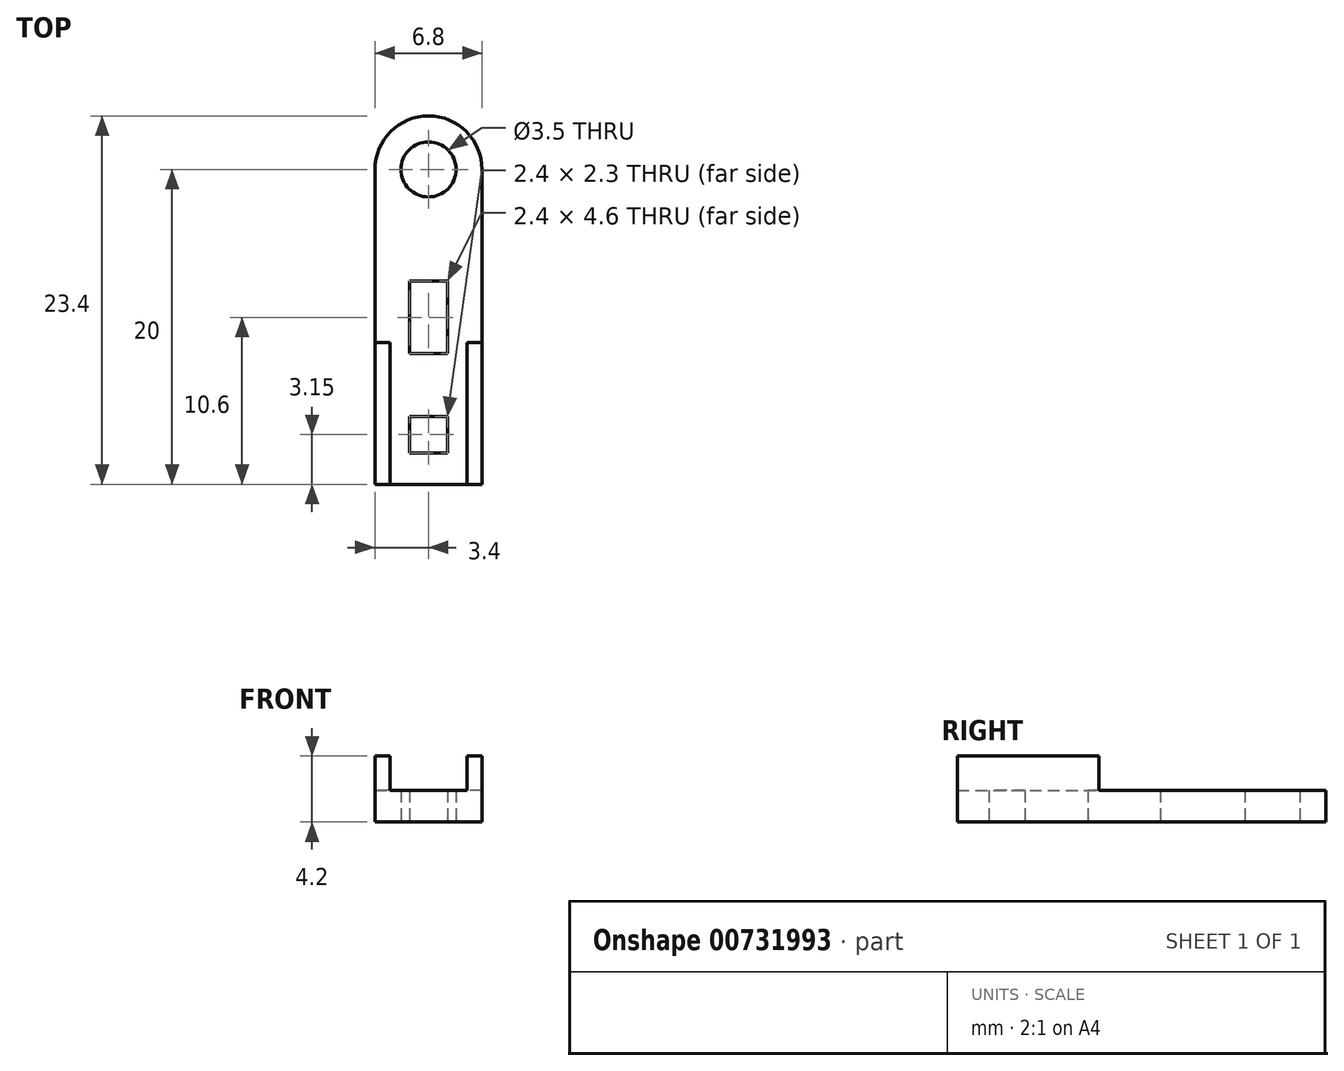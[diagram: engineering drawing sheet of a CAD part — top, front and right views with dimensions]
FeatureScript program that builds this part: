
annotation { "Feature Type Name" : "Feature", "Feature Type Description" : "" }
export const myFeature = defineFeature(function(context is Context, id is Id, definition is map)
    precondition{}
    {
        {
            var Q0;
            Q0=qCreatedBy(makeId("Top.planeOp"),FACE);
            var sketch = newSketch(context, id + "F0", { "sketchPlane" : qUnion([Q0])});
            skArc(sketch, "E0", {"start": v(3.4, 10) * mm, "mid": v(0, 13.4) * mm, "end": v(-3.4, 10) * mm});
            skLineSegment(sketch, "E1", {"start": v(-3.4, 10) * mm, "end": v(-3.4, -10) * mm});
            skLineSegment(sketch, "E2", {"start": v(-3.4, -10) * mm, "end": v(3.4, -10) * mm});
            skLineSegment(sketch, "E3", {"start": v(3.4, -10) * mm, "end": v(3.4, 10) * mm});
            skLineSegment(sketch, "E4.bottom", {"start": v(-1.2, 2.9) * mm, "end": v(1.2, 2.9) * mm});
            skLineSegment(sketch, "E4.top", {"start": v(-1.2, -1.7) * mm, "end": v(1.2, -1.7) * mm});
            skLineSegment(sketch, "E4.left", {"start": v(-1.2, 2.9) * mm, "end": v(-1.2, -1.7) * mm});
            skLineSegment(sketch, "E4.right", {"start": v(1.2, 2.9) * mm, "end": v(1.2, -1.7) * mm});
            skLineSegment(sketch, "E5.bottom", {"start": v(-1.2, -5.7) * mm, "end": v(1.2, -5.7) * mm});
            skLineSegment(sketch, "E5.top", {"start": v(-1.2, -8) * mm, "end": v(1.2, -8) * mm});
            skLineSegment(sketch, "E5.left", {"start": v(-1.2, -5.7) * mm, "end": v(-1.2, -8) * mm});
            skLineSegment(sketch, "E5.right", {"start": v(1.2, -5.7) * mm, "end": v(1.2, -8) * mm});
            skPoint(sketch, "E6", {"position": v(0, 2.9) * mm});
            skPoint(sketch, "E7", {"position": v(0, -8) * mm});
            skCircle(sketch, "E8", {"center": v(0, 10) * mm, "radius": 1.75 * mm});
            skPoint(sketch, "E9", {"position": v(-3.4, 0) * mm});
            skSolve(sketch);
        }
        {
            var Q0;
            Q0=makeQuery(id+"F0.imprint","IMPRINT",FACE,{"disambiguationData":[TD([[makeQuery(id+"F0.imprint","IMPRINT",EDGE,{"derivedFrom":sQuery(id+"F0.wireOp",EDGE,"E0")}),1.0]])]});
            extrude(context, id + "F1", {"entities" : qUnion([Q0]), "depth" : 2 * mm, "offsetDistance" : 25.4 * mm});
        }
        {
            var Q0;
            Q0=makeQuery(id+"F1.opExtrude","CAP_FACE",FACE,{"disambiguationData":[OSD([sQuery(id+"F0.wireOp",EDGE,"E0"),sQuery(id+"F0.wireOp",EDGE,"E1"),sQuery(id+"F0.wireOp",EDGE,"E2"),sQuery(id+"F0.wireOp",EDGE,"E3"),sQuery(id+"F0.wireOp",EDGE,"E4.bottom"),sQuery(id+"F0.wireOp",EDGE,"E4.top"),sQuery(id+"F0.wireOp",EDGE,"E4.left"),sQuery(id+"F0.wireOp",EDGE,"E4.right"),sQuery(id+"F0.wireOp",EDGE,"E5.bottom"),sQuery(id+"F0.wireOp",EDGE,"E5.top"),sQuery(id+"F0.wireOp",EDGE,"E5.left"),sQuery(id+"F0.wireOp",EDGE,"E5.right"),sQuery(id+"F0.wireOp",EDGE,"E8")])],"isStart":false});
            var sketch = newSketch(context, id + "F2", { "sketchPlane" : qUnion([Q0])});
            skLineSegment(sketch, "E10.bottom", {"start": v(-3.4, -10) * mm, "end": v(2.45, -10) * mm});
            skLineSegment(sketch, "E10.top", {"start": v(-3.4, -1) * mm, "end": v(2.45, -1) * mm});
            skLineSegment(sketch, "E10.left", {"start": v(-3.4, -10) * mm, "end": v(-3.4, -1) * mm});
            skLineSegment(sketch, "E10.right", {"start": v(2.45, -10) * mm, "end": v(2.45, -1) * mm});
            skLineSegment(sketch, "E11.bottom", {"start": v(3.4, -10) * mm, "end": v(-2.45, -10) * mm});
            skLineSegment(sketch, "E11.top", {"start": v(3.4, -1) * mm, "end": v(-2.45, -1) * mm});
            skLineSegment(sketch, "E11.left", {"start": v(3.4, -10) * mm, "end": v(3.4, -1) * mm});
            skLineSegment(sketch, "E11.right", {"start": v(-2.45, -10) * mm, "end": v(-2.45, -1) * mm});
            skSolve(sketch);
        }
        {
            var Q0;
            Q0=makeQuery(id+"F2.imprint","IMPRINT",FACE,{"disambiguationData":[TD([[makeQuery(id+"F2.imprint","IMPRINT",EDGE,{"derivedFrom":sQuery(id+"F2.wireOp",EDGE,"E11.bottom")}),1.0]])]});
            var Q1;
            Q1=makeQuery(id+"F2.imprint","IMPRINT",FACE,{"disambiguationData":[TD([[makeQuery(id+"F2.imprint","IMPRINT",EDGE,{"derivedFrom":sQuery(id+"F2.wireOp",EDGE,"E10.bottom")}),1.0]])]});
            extrude(context, id + "F3", {"entities" : qUnion([Q0, Q1]), "operationType" : NewBodyOperationType.ADD, "depth" : 2.2 * mm, "offsetDistance" : 25.4 * mm});
        }
    });
